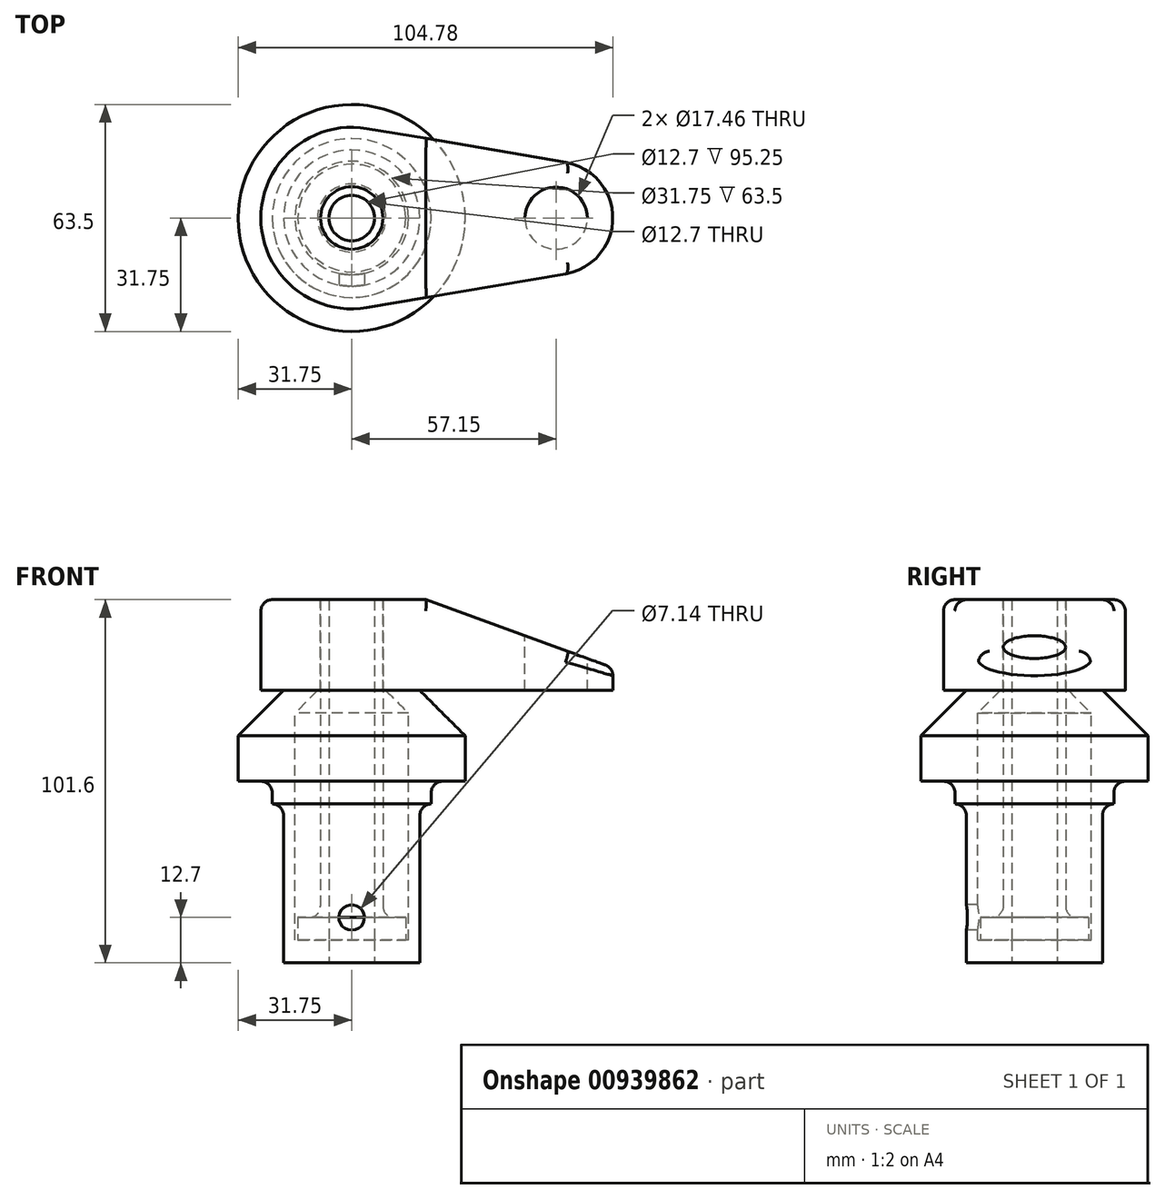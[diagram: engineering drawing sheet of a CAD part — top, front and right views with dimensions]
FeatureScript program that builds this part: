
annotation { "Feature Type Name" : "Feature", "Feature Type Description" : "" }
export const myFeature = defineFeature(function(context is Context, id is Id, definition is map)
    precondition{}
    {
        {
            var Q0;
            Q0=qCreatedBy(makeId("Front.planeOp"),FACE);
            var sketch = newSketch(context, id + "F0", { "sketchPlane" : qUnion([Q0])});
            skLineSegment(sketch, "E0", {"start": v(0, 0) * mm, "end": v(0, 76.2) * mm});
            skLineSegment(sketch, "E1", {"start": v(0, 76.2) * mm, "end": v(19.05, 76.2) * mm});
            skLineSegment(sketch, "E2", {"start": v(19.05, 76.2) * mm, "end": v(31.75, 63.5) * mm});
            skLineSegment(sketch, "E3", {"start": v(31.75, 63.5) * mm, "end": v(31.75, 50.8) * mm});
            skLineSegment(sketch, "E4", {"start": v(31.75, 50.8) * mm, "end": v(22.23, 50.8) * mm});
            skLineSegment(sketch, "E5", {"start": v(22.23, 50.8) * mm, "end": v(22.23, 44.45) * mm});
            skLineSegment(sketch, "E6", {"start": v(22.23, 44.45) * mm, "end": v(19.05, 44.45) * mm});
            skLineSegment(sketch, "E7", {"start": v(19.05, 44.45) * mm, "end": v(19.05, 0) * mm});
            skLineSegment(sketch, "E8", {"start": v(19.05, 0) * mm, "end": v(0, 0) * mm});
            skLineSegment(sketch, "E9", {"start": v(9.53, 76.2) * mm, "end": v(15.88, 69.85) * mm});
            skLineSegment(sketch, "E10", {"start": v(15.88, 69.85) * mm, "end": v(15.88, 6.35) * mm});
            skLineSegment(sketch, "E11", {"start": v(15.88, 6.35) * mm, "end": v(0, 6.35) * mm});
            skLineSegment(sketch, "E12", {"start": v(0, 76.2) * mm, "end": v(0, 94.21) * mm, "construction": true});
            skLineSegment(sketch, "E13", {"start": v(0, 76.2) * mm, "end": v(0, 101.6) * mm});
            skLineSegment(sketch, "E14", {"start": v(0, 101.6) * mm, "end": v(8.73, 101.6) * mm});
            skLineSegment(sketch, "E15", {"start": v(8.73, 101.6) * mm, "end": v(8.73, 12.7) * mm});
            skLineSegment(sketch, "E16", {"start": v(8.73, 12.7) * mm, "end": v(15.08, 12.7) * mm});
            skLineSegment(sketch, "E17", {"start": v(15.08, 12.7) * mm, "end": v(15.08, 6.35) * mm});
            skSolve(sketch);
        }
        {
            var Q0;
            {var subQ4=sQuery(id+"F0.wireOp",EDGE,"E2");Q0=makeQuery(id+"F0.imprint","IMPRINT",FACE,{"disambiguationData":[TD([[makeQuery(id+"F0.imprint","IMPRINT",EDGE,{"derivedFrom":subQ4}),-1.0]])]});}
            var Q1;
            Q1=sQuery(id+"F0.wireOp",EDGE,"E12");
            revolve(context, id + "F1", {"surfaceOperationType" : NewSurfaceOperationType.NEW, "entities" : qUnion([Q0]), "axis" : qUnion([Q1]), "revolveType" : RevolveType.FULL, "oppositeDirection" : true});
        }
        {
            var Q0;
            {var subQ0=sQuery(id+"F0.wireOp",EDGE,"E13");Q0=makeQuery(id+"F0.imprint","IMPRINT",FACE,{"disambiguationData":[TD([[makeQuery(id+"F0.imprint","IMPRINT",EDGE,{"derivedFrom":subQ0}),-1.0]])]});}
            var Q1;
            {var subQ0=sQuery(id+"F0.wireOp",EDGE,"E16");Q1=makeQuery(id+"F0.imprint","IMPRINT",FACE,{"disambiguationData":[TD([[makeQuery(id+"F0.imprint","IMPRINT",EDGE,{"derivedFrom":subQ0}),-1.0]])]});}
            var Q2;
            Q2=sQuery(id+"F0.wireOp",EDGE,"E13");
            revolve(context, id + "F2", {"surfaceOperationType" : NewSurfaceOperationType.NEW, "entities" : qUnion([Q0, Q1]), "axis" : qUnion([Q2]), "revolveType" : RevolveType.FULL});
        }
        {
            var Q0;
            Q0=makeQuery(id+"F2.opRevolve","SWEPT_FACE",FACE,{"disambiguationData":[OSD([sQuery(id+"F0.wireOp",EDGE,"E14")])]});
            var sketch = newSketch(context, id + "F3", { "sketchPlane" : qUnion([Q0])});
            skCircle(sketch, "E18", {"center": v(0, 0) * mm, "radius": 25.4 * mm});
            skCircle(sketch, "E19", {"center": v(57.15, 0) * mm, "radius": 15.88 * mm});
            skLineSegment(sketch, "E20", {"start": v(4.23, 25.04) * mm, "end": v(59.8, 15.65) * mm});
            skLineSegment(sketch, "E21", {"start": v(4.23, -25.04) * mm, "end": v(59.8, -15.65) * mm});
            skCircle(sketch, "E22.0", {"center": v(0, 0) * mm, "radius": 8.73 * mm});
            skCircle(sketch, "E23", {"center": v(57.15, 0) * mm, "radius": 8.73 * mm});
            skLineSegment(sketch, "E24", {"start": v(-25.4, 0) * mm, "end": v(73.03, 0) * mm, "construction": true});
            skSolve(sketch);
        }
        {
            var Q0;
            Q0 = qSketchRegion(id + "F3", true);
            var Q1;
            Q1=makeQuery(id+"F1.opRevolve","SWEPT_FACE",FACE,{"disambiguationData":[OSD([sQuery(id+"F0.wireOp",EDGE,"E1")])]});
            extrude(context, id + "F4", {"entities" : qUnion([Q0]), "endBound" : BoundingType.UP_TO_SURFACE, "oppositeDirection" : true, "depth" : 25.4 * mm, "endBoundEntityFace" : qUnion([Q1]), "offsetDistance" : 0.8 * mm});
        }
        {
            var Q0;
            Q0=qCreatedBy(makeId("Front.planeOp"),FACE);
            var sketch = newSketch(context, id + "F5", { "sketchPlane" : qUnion([Q0])});
            skLineSegment(sketch, "E25", {"start": v(20.69, 101.6) * mm, "end": v(73.03, 82.55) * mm});
            skLineSegment(sketch, "E26", {"start": v(73.03, 82.55) * mm, "end": v(73.03, 101.6) * mm});
            skLineSegment(sketch, "E27", {"start": v(73.03, 101.6) * mm, "end": v(20.69, 101.6) * mm});
            skSolve(sketch);
        }
        {
            var Q0;
            Q0 = qSketchRegion(id + "F5", true);
            extrude(context, id + "F6", {"entities" : qUnion([Q0]), "operationType" : NewBodyOperationType.REMOVE, "endBound" : BoundingType.THROUGH_ALL, "oppositeDirection" : true, "depth" : 25.4 * mm, "offsetDistance" : 25.4 * mm, "hasSecondDirection" : true, "secondDirectionBound" : BoundingType.THROUGH_ALL, "secondDirectionOppositeDirection" : false, "secondDirectionDepth" : 25.4 * mm});
        }
        {
            var Q0;
            Q0=qCreatedBy(makeId("Front.planeOp"),FACE);
            var sketch = newSketch(context, id + "F7", { "sketchPlane" : qUnion([Q0])});
            skPoint(sketch, "E28", {"position": v(0, 12.7) * mm});
            skSolve(sketch);
        }
        {
            var Q0;
            Q0=sQuery(id+"F7.wireOp",VERTEX,"E28");
            var Q1;
            Q1=makeQuery(id+"F1.opRevolve","SWEPT_BODY",BODY,{"disambiguationData":[OSD([sQuery(id+"F0.wireOp",EDGE,"E0"),sQuery(id+"F0.wireOp",EDGE,"E1"),sQuery(id+"F0.wireOp",EDGE,"E2"),sQuery(id+"F0.wireOp",EDGE,"E3"),sQuery(id+"F0.wireOp",EDGE,"E4"),sQuery(id+"F0.wireOp",EDGE,"E5"),sQuery(id+"F0.wireOp",EDGE,"E6"),sQuery(id+"F0.wireOp",EDGE,"E7"),sQuery(id+"F0.wireOp",EDGE,"E8"),sQuery(id+"F0.wireOp",EDGE,"E9"),sQuery(id+"F0.wireOp",EDGE,"E10"),sQuery(id+"F0.wireOp",EDGE,"E11")])]});
            hole(context, id + "F8", {"style" : HoleStyle.SIMPLE, "endStyle" : HoleEndStyle.THROUGH, "oppositeDirection" : true, "standardTappedOrClearance" : lookupTablePath({ "fit" : "Normal (ASME)", "standard" : "ANSI", "size" : "1/4", "type" : "Clearance" }), "standardBlindInLast" : lookupTablePath({ "fit" : "Normal", "standard" : "ANSI", "engagement" : "75%", "pitch" : "20 tpi", "size" : "1/4", "type" : "Clearance & tapped" }), "holeDiameter" : 7.14 * mm, "majorDiameter" : 6.35 * mm, "tappedDepth" : 14.3 * mm, "tapClearance" : 3, "locations" : qUnion([Q0]), "scope" : qUnion([Q1]), "startStyle" : HoleStartStyle.PART});
        }
        {
            var Q0;
            Q0=makeQuery(id+"F6.boolean.opBoolean","INTERSECT",EDGE,{"derivedFrom":[makeQuery(id+"F4.opExtrude","SWEPT_FACE",FACE,{"disambiguationData":[OSD([sQuery(id+"F3.wireOp",EDGE,"E21")])]}),makeQuery(id+"F6.opExtrude","SWEPT_FACE",FACE,{"disambiguationData":[OSD([sQuery(id+"F5.wireOp",EDGE,"E25")])]})]});
            var Q1;
            Q1=makeQuery(id+"F4.opExtrude","CAP_EDGE",EDGE,{"disambiguationData":[OSD([sQuery(id+"F3.wireOp",EDGE,"E18")])],"isStart":true});
            var Q2;
            Q2=makeQuery(id+"F6.boolean.opBoolean","COPY",EDGE,{"derivedFrom":makeQuery(id+"F6.opExtrude","SWEPT_EDGE",EDGE,{"disambiguationData":[OSD([sQuery(id+"F5.wireOp",EDGE,"E25"),sQuery(id+"F5.wireOp",EDGE,"E27")])]})});
            var Q3;
            Q3=makeQuery(id+"F1.opRevolve","SWEPT_EDGE",EDGE,{"disambiguationData":[OSD([sQuery(id+"F0.wireOp",EDGE,"E4"),sQuery(id+"F0.wireOp",EDGE,"E5")])]});
            var Q4;
            Q4=makeQuery(id+"F1.opRevolve","SWEPT_EDGE",EDGE,{"disambiguationData":[OSD([sQuery(id+"F0.wireOp",EDGE,"E6"),sQuery(id+"F0.wireOp",EDGE,"E7")])]});
            var Q5;
            Q5=makeQuery(id+"F2.opRevolve","SWEPT_EDGE",EDGE,{"disambiguationData":[OSD([sQuery(id+"F0.wireOp",EDGE,"E15"),sQuery(id+"F0.wireOp",EDGE,"E16")])]});
            fillet(context, id + "F9", {"entities" : qUnion([Q0, Q1, Q2, Q3, Q4, Q5]), "radius" : 3.17 * mm, "tangentPropagation" : true, "allowEdgeOverflow" : false});
        }
        {
            var Q0;
            Q0=makeQuery(id+"F1.opRevolve","SWEPT_FACE",FACE,{"disambiguationData":[OSD([sQuery(id+"F0.wireOp",EDGE,"E8")])]});
            var sketch = newSketch(context, id + "F10", { "sketchPlane" : qUnion([Q0])});
            skCircle(sketch, "E29", {"center": v(0, 0) * mm, "radius": 6.35 * mm});
            skSolve(sketch);
        }
        {
            var Q0;
            Q0 = qSketchRegion(id + "F10", true);
            extrude(context, id + "F11", {"entities" : qUnion([Q0]), "operationType" : NewBodyOperationType.REMOVE, "endBound" : BoundingType.THROUGH_ALL, "oppositeDirection" : true, "depth" : 25.4 * mm, "offsetDistance" : 25.4 * mm});
        }
    });
